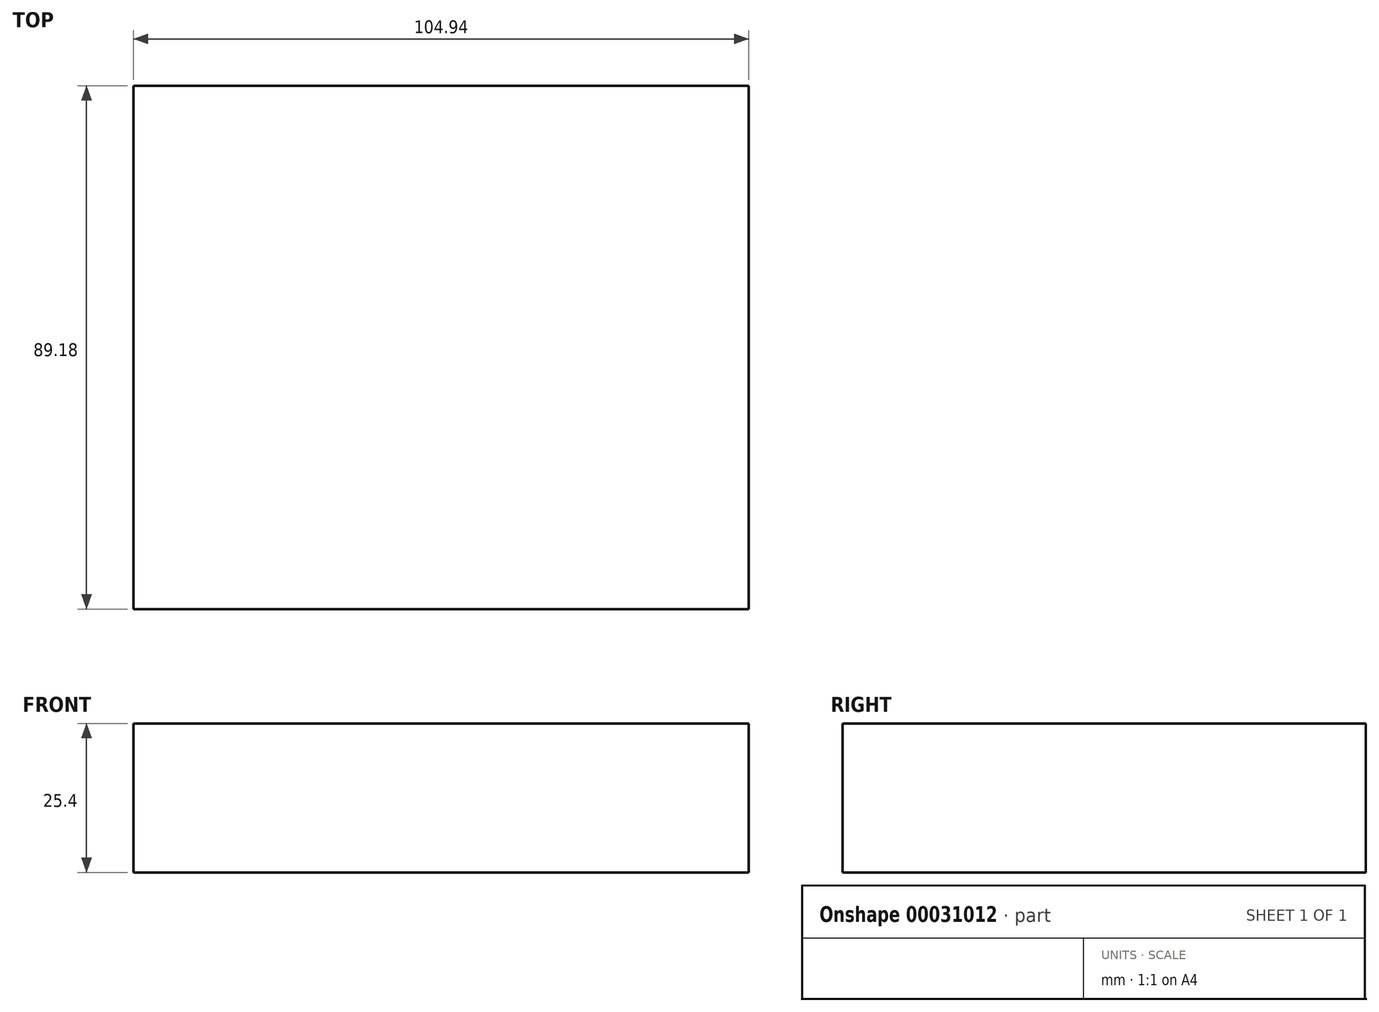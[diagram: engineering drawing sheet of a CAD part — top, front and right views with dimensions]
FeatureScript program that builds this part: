
annotation { "Feature Type Name" : "Feature", "Feature Type Description" : "" }
export const myFeature = defineFeature(function(context is Context, id is Id, definition is map)
    precondition{}
    {
        {
            var Q0;
            Q0=qCreatedBy(makeId("Top.planeOp"),FACE);
            var sketch = newSketch(context, id + "F0", { "sketchPlane" : qUnion([Q0])});
            skLineSegment(sketch, "E0.rect.bottom", {"start": v(52.47, 44.6) * mm, "end": v(-52.47, 44.6) * mm});
            skLineSegment(sketch, "E0.rect.top", {"start": v(52.47, -44.6) * mm, "end": v(-52.47, -44.6) * mm});
            skLineSegment(sketch, "E0.rect.left", {"start": v(52.47, 44.6) * mm, "end": v(52.47, -44.6) * mm});
            skLineSegment(sketch, "E0.rect.right", {"start": v(-52.47, 44.6) * mm, "end": v(-52.47, -44.6) * mm});
            skPoint(sketch, "E0.rect.middle", {"position": v(0, 0) * mm});
            skSolve(sketch);
        }
        {
            var Q0;
            Q0=makeQuery(id+"F0.imprint","IMPRINT",FACE,{"disambiguationData":[TD([[makeQuery(id+"F0.imprint","IMPRINT",EDGE,{"derivedFrom":sQuery(id+"F0.wireOp",EDGE,"E0.rect.bottom")}),1.0]])]});
            extrude(context, id + "F1", {"entities" : qUnion([Q0]), "depth" : 25.4 * mm});
        }
    });
